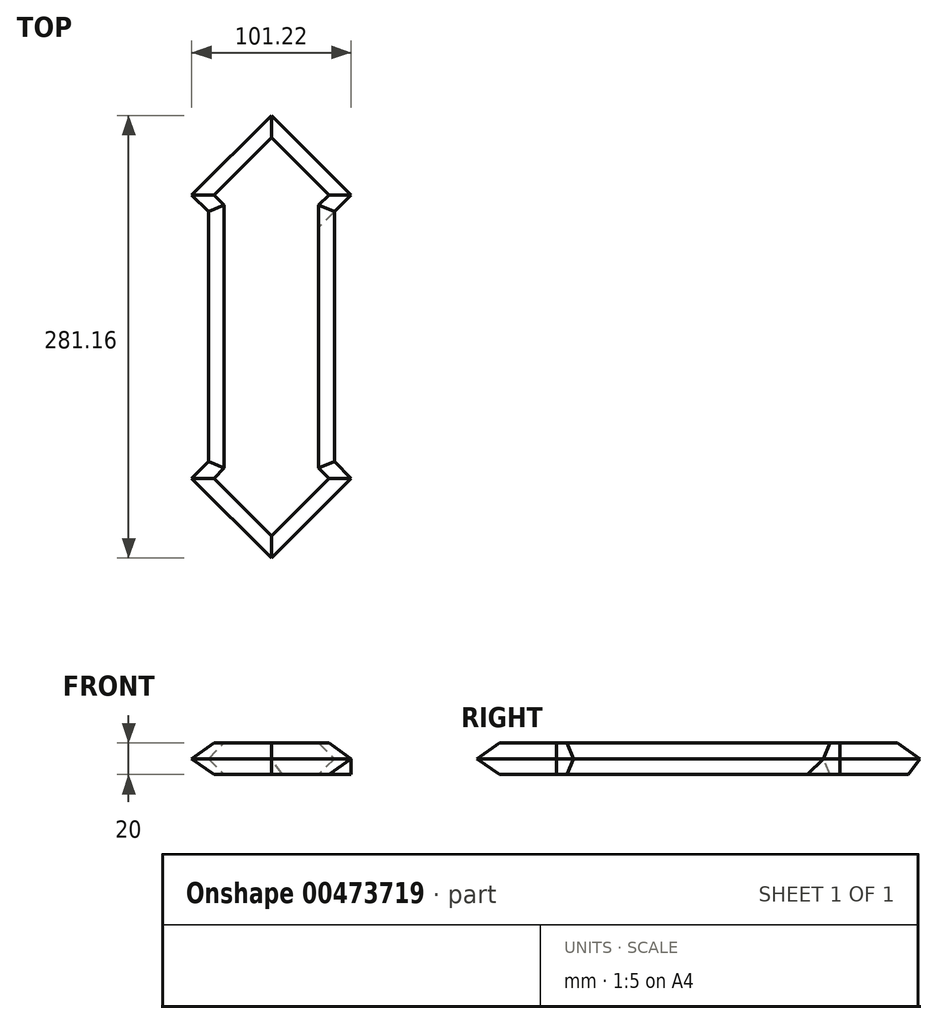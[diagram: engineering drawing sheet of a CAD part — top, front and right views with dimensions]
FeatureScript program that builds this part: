
annotation { "Feature Type Name" : "Feature", "Feature Type Description" : "" }
export const myFeature = defineFeature(function(context is Context, id is Id, definition is map)
    precondition{}
    {
        {
            var Q0;
            Q0=qCreatedBy(makeId("Top.planeOp"),FACE);
            var sketch = newSketch(context, id + "F0", { "sketchPlane" : qUnion([Q0])});
            skLineSegment(sketch, "E0", {"start": v(0, 0) * mm, "end": v(-40, 0) * mm, "construction": true});
            skLineSegment(sketch, "E1", {"start": v(-40, 0) * mm, "end": v(-50.6, 10.6) * mm});
            skLineSegment(sketch, "E2", {"start": v(-50.6, 10.6) * mm, "end": v(0, 61.21) * mm});
            skLineSegment(sketch, "E3", {"start": v(-40, 0) * mm, "end": v(-40, -79.37) * mm});
            skLineSegment(sketch, "E4", {"start": v(0, 61.21) * mm, "end": v(0, -71.85) * mm, "construction": true});
            skLineSegment(sketch, "E5.MirrorCS", {"start": v(40, 0) * mm, "end": v(40, -79.37) * mm});
            skLineSegment(sketch, "E6.MirrorCS", {"start": v(40, 0) * mm, "end": v(50.6, 10.6) * mm});
            skLineSegment(sketch, "E7.MirrorCS", {"start": v(50.6, 10.6) * mm, "end": v(0, 61.21) * mm});
            skLineSegment(sketch, "E8", {"start": v(-40, -79.37) * mm, "end": v(40, -79.37) * mm});
            skLineSegment(sketch, "E9.MirrorCS", {"start": v(40, -158.73) * mm, "end": v(40, -79.37) * mm});
            skLineSegment(sketch, "E10.MirrorCS", {"start": v(50.6, -169.34) * mm, "end": v(0, -219.95) * mm});
            skLineSegment(sketch, "E11.MirrorCS", {"start": v(40, -158.73) * mm, "end": v(50.6, -169.34) * mm});
            skLineSegment(sketch, "E12.MirrorCS", {"start": v(-50.6, -169.34) * mm, "end": v(0, -219.95) * mm});
            skLineSegment(sketch, "E13.MirrorCS", {"start": v(-40, -158.73) * mm, "end": v(-50.6, -169.34) * mm});
            skLineSegment(sketch, "E14.MirrorCS", {"start": v(-40, -158.73) * mm, "end": v(-40, -79.37) * mm});
            skSolve(sketch);
        }
        {
            var Q0;
            Q0 = qSketchRegion(id + "F0", true);
            extrude(context, id + "F1", {"entities" : qUnion([Q0]), "depth" : 20 * mm});
        }
        {
            var Q0;
            Q0=makeQuery(id+"F1.opExtrude","CAP_EDGE",EDGE,{"disambiguationData":[OSD([sQuery(id+"F0.wireOp",EDGE,"E5.MirrorCS"),sQuery(id+"F0.wireOp",EDGE,"E9.MirrorCS")])],"isStart":false});
            var Q1;
            Q1=makeQuery(id+"F1.opExtrude","CAP_EDGE",EDGE,{"disambiguationData":[OSD([sQuery(id+"F0.wireOp",EDGE,"E7.MirrorCS")])],"isStart":false});
            var Q2;
            Q2=makeQuery(id+"F1.opExtrude","CAP_EDGE",EDGE,{"disambiguationData":[OSD([sQuery(id+"F0.wireOp",EDGE,"E2")])],"isStart":false});
            var Q3;
            Q3=makeQuery(id+"F1.opExtrude","CAP_EDGE",EDGE,{"disambiguationData":[OSD([sQuery(id+"F0.wireOp",EDGE,"E1")])],"isStart":false});
            var Q4;
            Q4=makeQuery(id+"F1.opExtrude","CAP_EDGE",EDGE,{"disambiguationData":[OSD([sQuery(id+"F0.wireOp",EDGE,"E6.MirrorCS")])],"isStart":false});
            var Q5;
            Q5=makeQuery(id+"F1.opExtrude","CAP_EDGE",EDGE,{"disambiguationData":[OSD([sQuery(id+"F0.wireOp",EDGE,"E3"),sQuery(id+"F0.wireOp",EDGE,"E14.MirrorCS")])],"isStart":false});
            var Q6;
            Q6=makeQuery(id+"F1.opExtrude","CAP_EDGE",EDGE,{"disambiguationData":[OSD([sQuery(id+"F0.wireOp",EDGE,"E13.MirrorCS")])],"isStart":false});
            var Q7;
            Q7=makeQuery(id+"F1.opExtrude","CAP_EDGE",EDGE,{"disambiguationData":[OSD([sQuery(id+"F0.wireOp",EDGE,"E12.MirrorCS")])],"isStart":false});
            var Q8;
            Q8=makeQuery(id+"F1.opExtrude","CAP_EDGE",EDGE,{"disambiguationData":[OSD([sQuery(id+"F0.wireOp",EDGE,"E10.MirrorCS")])],"isStart":false});
            var Q9;
            Q9=makeQuery(id+"F1.opExtrude","CAP_EDGE",EDGE,{"disambiguationData":[OSD([sQuery(id+"F0.wireOp",EDGE,"E11.MirrorCS")])],"isStart":false});
            var Q10;
            Q10=makeQuery(id+"F1.opExtrude","CAP_EDGE",EDGE,{"disambiguationData":[OSD([sQuery(id+"F0.wireOp",EDGE,"E5.MirrorCS"),sQuery(id+"F0.wireOp",EDGE,"E9.MirrorCS")])],"isStart":true});
            var Q11;
            Q11=makeQuery(id+"F1.opExtrude","CAP_EDGE",EDGE,{"disambiguationData":[OSD([sQuery(id+"F0.wireOp",EDGE,"E10.MirrorCS")])],"isStart":true});
            var Q12;
            Q12=makeQuery(id+"F1.opExtrude","CAP_EDGE",EDGE,{"disambiguationData":[OSD([sQuery(id+"F0.wireOp",EDGE,"E11.MirrorCS")])],"isStart":true});
            var Q13;
            Q13=makeQuery(id+"F1.opExtrude","CAP_EDGE",EDGE,{"disambiguationData":[OSD([sQuery(id+"F0.wireOp",EDGE,"E12.MirrorCS")])],"isStart":true});
            var Q14;
            Q14=makeQuery(id+"F1.opExtrude","CAP_EDGE",EDGE,{"disambiguationData":[OSD([sQuery(id+"F0.wireOp",EDGE,"E13.MirrorCS")])],"isStart":true});
            var Q15;
            Q15=makeQuery(id+"F1.opExtrude","CAP_EDGE",EDGE,{"disambiguationData":[OSD([sQuery(id+"F0.wireOp",EDGE,"E3"),sQuery(id+"F0.wireOp",EDGE,"E14.MirrorCS")])],"isStart":true});
            var Q16;
            Q16=makeQuery(id+"F1.opExtrude","CAP_EDGE",EDGE,{"disambiguationData":[OSD([sQuery(id+"F0.wireOp",EDGE,"E1")])],"isStart":true});
            var Q17;
            Q17=makeQuery(id+"F1.opExtrude","CAP_EDGE",EDGE,{"disambiguationData":[OSD([sQuery(id+"F0.wireOp",EDGE,"E2")])],"isStart":true});
            chamfer(context, id + "F2", {"entities" : qUnion([Q0, Q1, Q2, Q3, Q4, Q5, Q6, Q7, Q8, Q9, Q10, Q11, Q12, Q13, Q14, Q15, Q16, Q17]), "chamferType" : ChamferType.OFFSET_ANGLE, "width" : 10 * mm, "oppositeDirection" : false, "angle" : 45 * degree, "tangentPropagation" : true});
        }
    });
